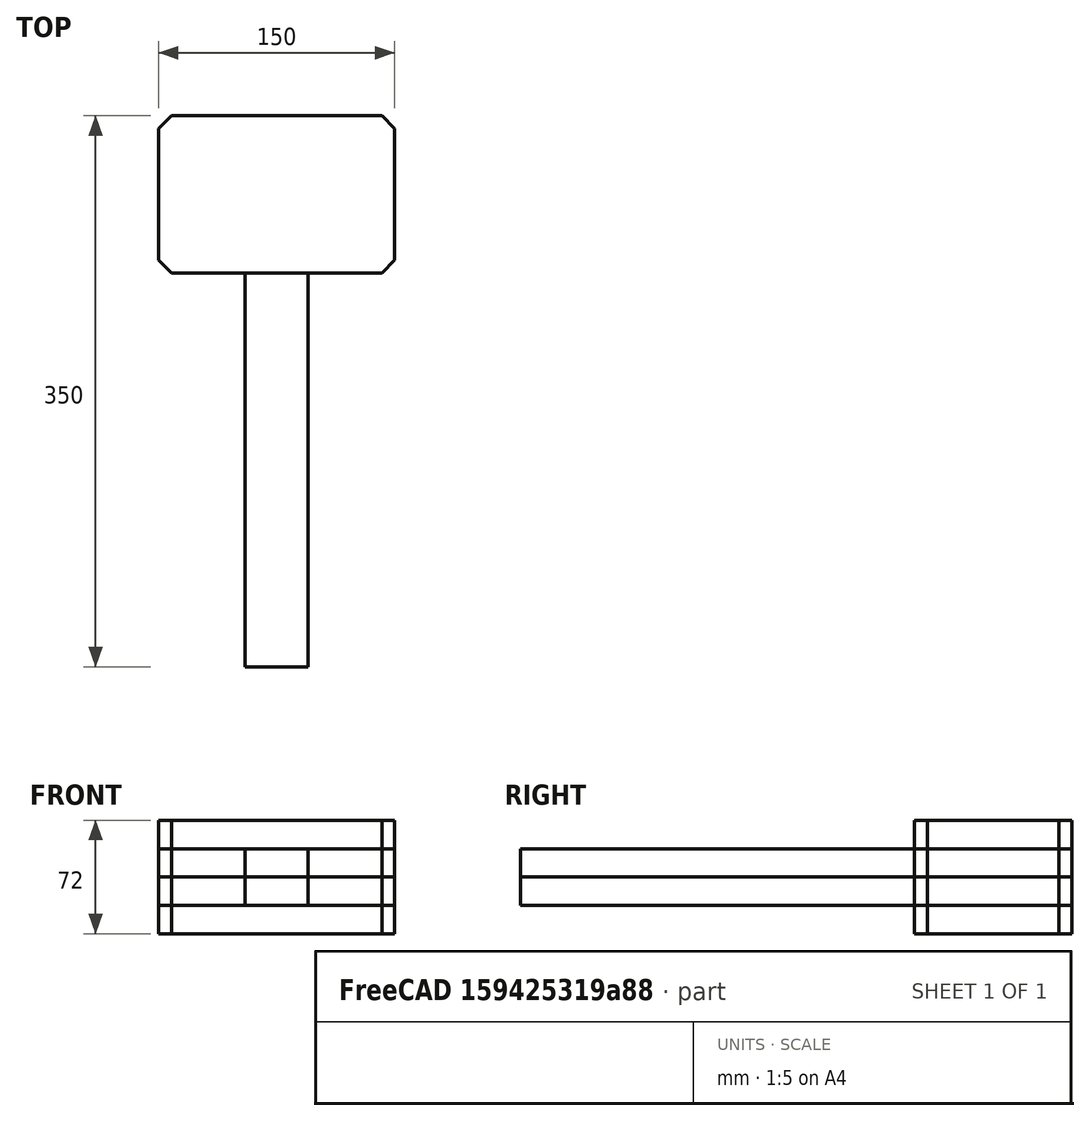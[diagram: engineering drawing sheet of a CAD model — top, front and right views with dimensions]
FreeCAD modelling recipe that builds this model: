
FCSTD DOCUMENT  (FreeCAD 0.17R10402 (Git))
Label: Mallet
License: All rights reserved
LicenseURL: http://en.wikipedia.org/wiki/All_rights_reserved
objects: Part::FeaturePython×3, Part::Part2DObjectPython×2
note: 5 computed .brp shape members not serialized (recipe doc carries the construction recipe); baked Part::Feature solids carry a one-line shape summary decoded from their .brp

FEATURE [Part::Part2DObjectPython] DWire  # Draft 2D object (typed FeaturePython)
  ChamferSize = 0
  Closed = true
  End = (-5339.89,5803.84,0)
  FilletRadius = 0
  Length = 980.748
  MakeFace = true
  Points = (12) [(-5206.32,5803.84,0),(-5198.1,5795.63,0),(-5198.1,5712.06,0),(-5206.32,5703.84,0),(-5253.1,5703.84,0),(-5253.1,5453.84,0),(-5293.1,5453.84,0),+5 more]
  Start = (-5206.32,5803.84,0)
  Subdivisions = 0
FEATURE [Part::Part2DObjectPython] DWire001  # Draft 2D object (typed FeaturePython)
  ChamferSize = 0
  Closed = true
  End = (-5348.1,5712.06,0)
  FilletRadius = 0
  Length = 480.748
  MakeFace = true
  Points = (8) [(-5348.1,5795.63,0),(-5339.89,5803.84,0),(-5206.32,5803.84,0),(-5198.1,5795.63,0),(-5198.1,5712.06,0),(-5206.32,5703.84,0),(-5339.89,5703.84,0),+1 more]
  Start = (-5348.1,5795.63,0)
  Subdivisions = 0
FEATURE [Part::FeaturePython] Panel  label="Mallet core"  # WARN: FeaturePython — macro-defined, semantics opaque (R4)
  Area = 24865
  Base = -> DWire
  FaceMaker = 0
  HorizontalArea = 0
  Length = 0
  MoveWithHost = false
  Normal = (0,0,1)
  PerimeterLength = 0
  Role = 0
  Sheets = 2
  Thickness = 18
  VerticalArea = 0
  WaveDirection = 0
  WaveHeight = 0
  WaveLength = 0
  WaveType = 0
  Width = 0
FEATURE [Part::FeaturePython] Panel001  label="Mallet side 1"  # WARN: FeaturePython — macro-defined, semantics opaque (R4)
  Area = 14865
  Base = -> DWire001
  FaceMaker = 0
  HorizontalArea = 0
  Length = 0
  MoveWithHost = false
  Normal = (0,0,0)
  PerimeterLength = 0
  Role = 0
  Sheets = 1
  Thickness = 18
  VerticalArea = 0
  WaveDirection = 0
  WaveHeight = 0
  WaveLength = 0
  WaveType = 0
  Width = 0
FEATURE [Part::FeaturePython] Panel002  label="Mallet side 2"  # WARN: FeaturePython — macro-defined, semantics opaque (R4)
  Area = 14865
  CloneOf = -> Panel001
  FaceMaker = 0
  HorizontalArea = 0
  Length = 0
  MoveWithHost = false
  Normal = (0,0,0)
  PerimeterLength = 0
  Placement = pos=(0,0,54) rot=(0,0,1;0rad)
  Role = 0
  Sheets = 1
  Thickness = 18
  VerticalArea = 0
  WaveDirection = 0
  WaveHeight = 0
  WaveLength = 0
  WaveType = 0
  Width = 0
